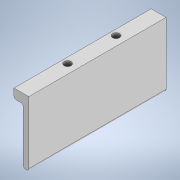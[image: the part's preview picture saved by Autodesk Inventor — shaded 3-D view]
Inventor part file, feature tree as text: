
AUTODESK INVENTOR PART (.ipt)
format: ipt  version: 2020 (Build 240168000, 168)  size: 169,472 bytes
history: native  units: mm
features: extrude x5, sketch x5, fillet x1
ambient origin geometry x8: Origin, YZ Plane, XZ Plane, XY Plane, X Axis, Y Axis, Z Axis, Center Point
bodies: Solid1 (feature_tree)
feature tree (11):
  extrude  "Extrusion1"  Depth=28.25mm
  extrude  "Extrusion7"  Depth=60.0mm TaperAngle=0.0deg
  extrude  "Extrusion8"  Depth=3.1mm
  extrude  "Extrusion9"  Depth=21.2mm
  extrude  "Extrusion10"  Depth=0.5mm
  fillet  "Fillet1"  Radius=2.0mm
  sketch  "Sketch1"  dims[d0=8.0mm d1=28.25mm]
  sketch  "Sketch8"  dims[d2=60.0mm d3=0.0mm d42=1.5mm d43=0.0mm]
  sketch  "Sketch9"  dims[d44=3.1mm d45=3.1mm]
  sketch  "Sketch11"  dims[d46=21.2mm d47=2.5mm]
  sketch  "Sketch12"  dims[d48=2.5mm d49=17.85mm d53=2.0mm d54=0.0mm d55=4.0mm d56=4.0mm d57=4.0mm d58=4.0mm d59=2.0mm d60=0.0mm d61=4.05mm d62=4.0mm d63=24.25mm d64=0.0mm d65=0.0mm d66=1.0mm d22=0.5mm d23=0.872665mm d24=0.5mm d25=0.872665mm]
